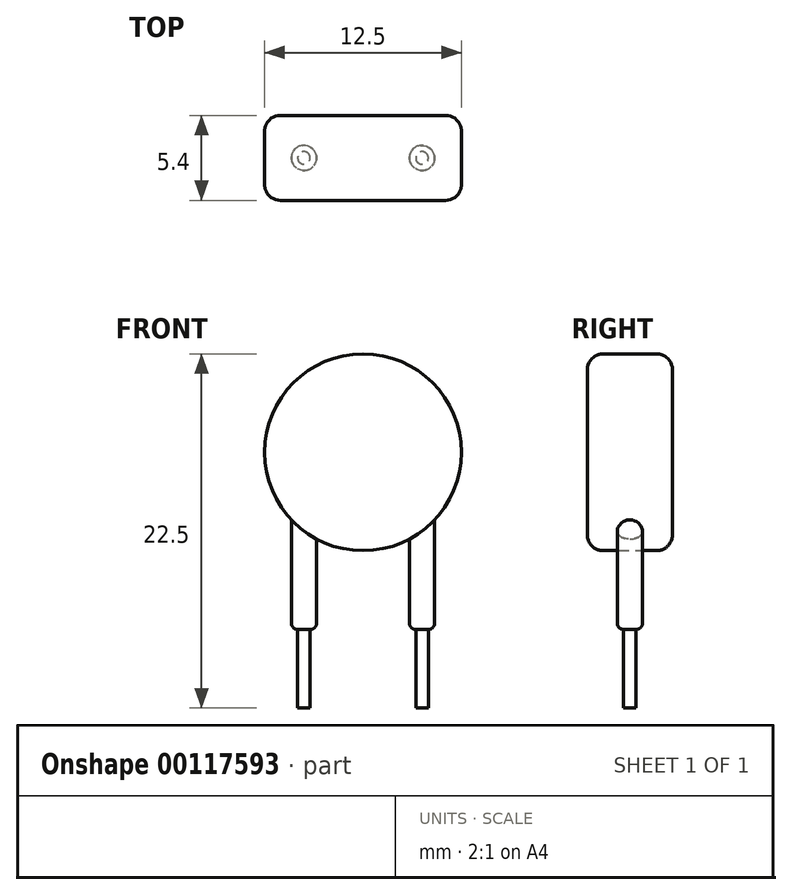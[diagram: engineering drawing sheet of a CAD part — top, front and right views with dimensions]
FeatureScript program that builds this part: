
annotation { "Feature Type Name" : "Feature", "Feature Type Description" : "" }
export const myFeature = defineFeature(function(context is Context, id is Id, definition is map)
    precondition{}
    {
        {
            var Q0;
            Q0=qCreatedBy(makeId("Front.planeOp"),FACE);
            var sketch = newSketch(context, id + "F0", { "sketchPlane" : qUnion([Q0])});
            skCircle(sketch, "E0", {"center": v(0, 11.25) * mm, "radius": 6.25 * mm});
            skSolve(sketch);
        }
        {
            var Q0;
            {var subQ0=sQuery(id+"F0.wireOp",EDGE,"E0");var subQ1=makeQuery(id+"F0.imprint","INTERSECT",VERTEX,{"derivedFrom":[subQ0,sQuery(id+"F0.wireOp",EDGE,"s0oEZiCd-AtFq-xSFY-pKhv-9fTZynv1yewS")]});Q0=makeQuery(id+"F0.imprint","IMPRINT",FACE,{"disambiguationData":[TD([[makeQuery(id+"F0.imprint","IMPRINT",EDGE,{"disambiguationData":[TD([[subQ1,-1.0]])],"derivedFrom":subQ0}),1.0]])]});}
            var Q1;
            Q1=makeQuery(id+"F0.imprint","IMPRINT",FACE,{"disambiguationData":[TD([[makeQuery(id+"F0.imprint","IMPRINT",EDGE,{"derivedFrom":sQuery(id+"F0.wireOp",EDGE,"E0")}),1.0]])]});
            extrude(context, id + "F1", {"entities" : qUnion([Q0, Q1]), "endBound" : BoundingType.SYMMETRIC, "depth" : 5.4 * mm});
        }
        {
            var Q0;
            Q0=qCreatedBy(makeId("Top.planeOp"),FACE);
            var sketch = newSketch(context, id + "F2", { "sketchPlane" : qUnion([Q0])});
            skCircle(sketch, "E1", {"center": v(-3.75, 0) * mm, "radius": 0.8 * mm});
            skCircle(sketch, "E2", {"center": v(3.75, 0) * mm, "radius": 0.8 * mm});
            skLineSegment(sketch, "E3", {"start": v(-3.75, 0) * mm, "end": v(3.75, 0) * mm, "construction": true});
            skCircle(sketch, "E4", {"center": v(-3.75, 0) * mm, "radius": 0.4 * mm});
            skCircle(sketch, "E5", {"center": v(3.75, 0) * mm, "radius": 0.4 * mm});
            skSolve(sketch);
        }
        {
            var Q0;
            Q0=makeQuery(id+"F2.imprint","IMPRINT",FACE,{"disambiguationData":[TD([[makeQuery(id+"F2.imprint","IMPRINT",EDGE,{"derivedFrom":sQuery(id+"F2.wireOp",EDGE,"E1")}),1.0]])]});
            var Q1;
            Q1=makeQuery(id+"F2.imprint","IMPRINT",FACE,{"disambiguationData":[TD([[makeQuery(id+"F2.imprint","IMPRINT",EDGE,{"derivedFrom":sQuery(id+"F2.wireOp",EDGE,"E2")}),1.0]])]});
            var Q2;
            Q2=makeQuery(id+"F2.imprint","IMPRINT",FACE,{"disambiguationData":[TD([[makeQuery(id+"F2.imprint","IMPRINT",EDGE,{"derivedFrom":sQuery(id+"F2.wireOp",EDGE,"E4")}),1.0]])]});
            var Q3;
            Q3=makeQuery(id+"F2.imprint","IMPRINT",FACE,{"disambiguationData":[TD([[makeQuery(id+"F2.imprint","IMPRINT",EDGE,{"derivedFrom":sQuery(id+"F2.wireOp",EDGE,"E5")}),1.0]])]});
            extrude(context, id + "F3", {"entities" : qUnion([Q0, Q1, Q2, Q3]), "operationType" : NewBodyOperationType.ADD, "endBound" : BoundingType.UP_TO_NEXT, "depth" : 25 * mm});
        }
        {
            var Q0;
            Q0=makeQuery(id+"F2.imprint","IMPRINT",FACE,{"disambiguationData":[TD([[makeQuery(id+"F2.imprint","IMPRINT",EDGE,{"derivedFrom":sQuery(id+"F2.wireOp",EDGE,"E4")}),1.0]])]});
            var Q1;
            Q1=makeQuery(id+"F2.imprint","IMPRINT",FACE,{"disambiguationData":[TD([[makeQuery(id+"F2.imprint","IMPRINT",EDGE,{"derivedFrom":sQuery(id+"F2.wireOp",EDGE,"E5")}),1.0]])]});
            extrude(context, id + "F4", {"entities" : qUnion([Q0, Q1]), "operationType" : NewBodyOperationType.ADD, "oppositeDirection" : true, "depth" : 5 * mm});
        }
        {
            var Q0;
            Q0=makeQuery(id+"F3.opExtrude","CAP_EDGE",EDGE,{"disambiguationData":[OSD([sQuery(id+"F2.wireOp",EDGE,"E1")])],"isStart":true});
            var Q1;
            Q1=makeQuery(id+"F3.opExtrude","CAP_EDGE",EDGE,{"disambiguationData":[OSD([sQuery(id+"F2.wireOp",EDGE,"E2")])],"isStart":true});
            fillet(context, id + "F5", {"entities" : qUnion([Q0, Q1]), "radius" : 0.4 * mm, "tangentPropagation" : true, "allowEdgeOverflow" : false});
        }
        {
            var Q0;
            Q0=makeQuery(id+"F1.opExtrude","CAP_EDGE",EDGE,{"disambiguationData":[OSD([sQuery(id+"F0.wireOp",EDGE,"E0")])],"isStart":false});
            var Q1;
            Q1=makeQuery(id+"F1.opExtrude","CAP_EDGE",EDGE,{"disambiguationData":[OSD([sQuery(id+"F0.wireOp",EDGE,"E0")])],"isStart":true});
            fillet(context, id + "F6", {"entities" : qUnion([Q0, Q1]), "radius" : 1 * mm, "tangentPropagation" : true, "allowEdgeOverflow" : false});
        }
    });
